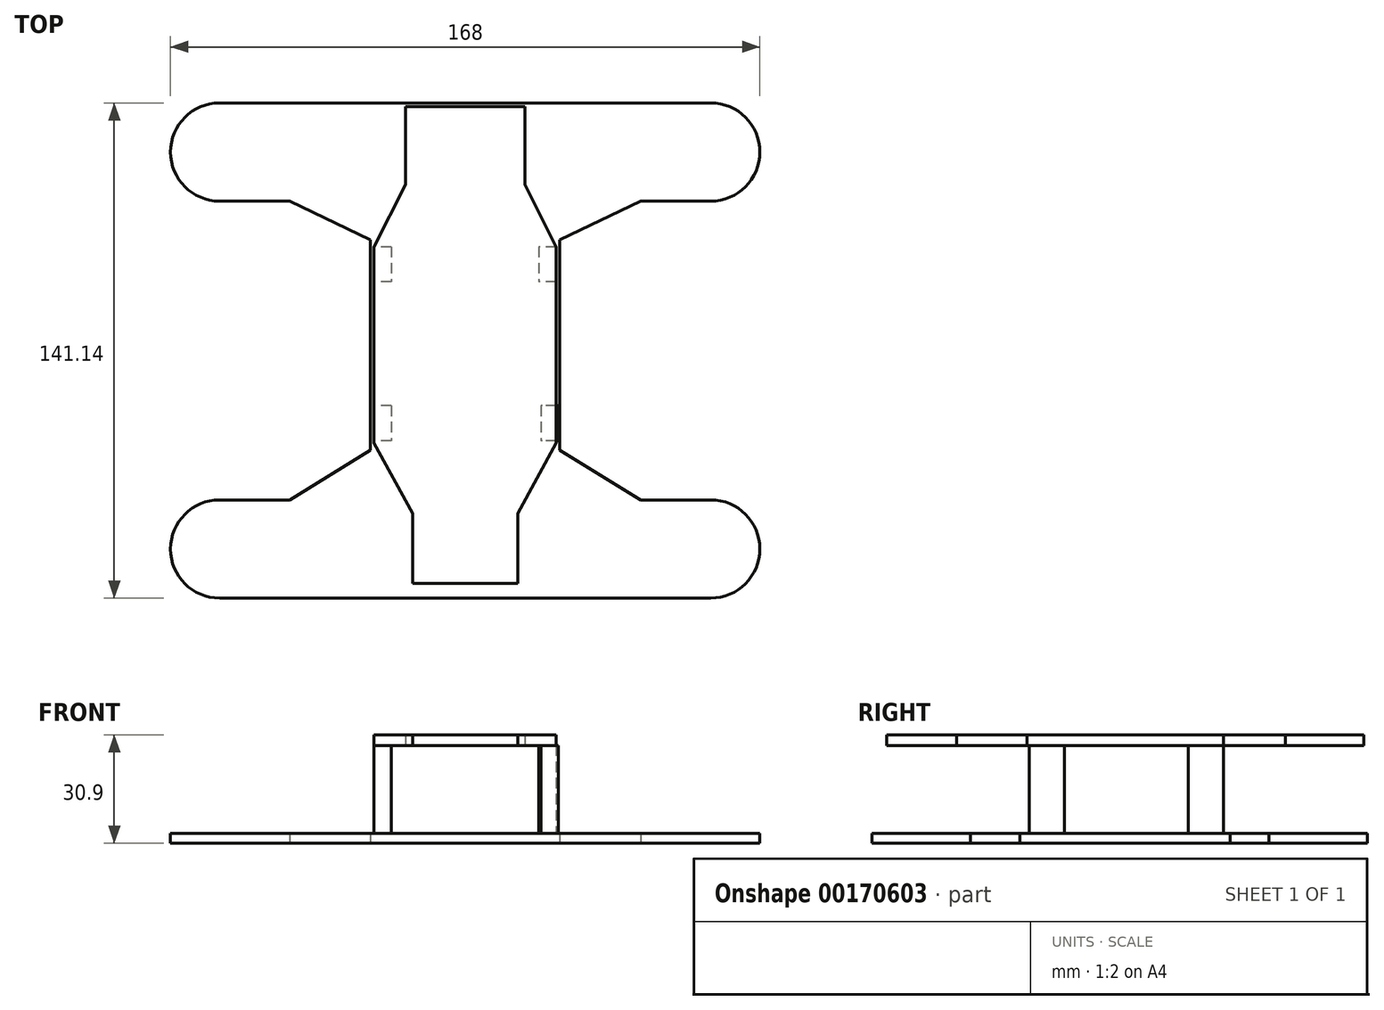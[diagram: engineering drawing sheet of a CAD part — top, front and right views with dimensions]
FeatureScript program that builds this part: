
annotation { "Feature Type Name" : "Feature", "Feature Type Description" : "" }
export const myFeature = defineFeature(function(context is Context, id is Id, definition is map)
    precondition{}
    {
        {
            var Q0;
            Q0=qCreatedBy(makeId("Top.planeOp"),FACE);
            var sketch = newSketch(context, id + "F0", { "sketchPlane" : qUnion([Q0])});
            skArc(sketch, "E0", {"start": v(-70, 69) * mm, "mid": v(-84, 55) * mm, "end": v(-70, 41) * mm});
            skArc(sketch, "E1", {"start": v(70, 41) * mm, "mid": v(84, 55) * mm, "end": v(70, 69) * mm});
            skArc(sketch, "E2", {"start": v(70, -72.14) * mm, "mid": v(84, -58.14) * mm, "end": v(70, -44.14) * mm});
            skArc(sketch, "E3", {"start": v(-70, -44.14) * mm, "mid": v(-84, -58.14) * mm, "end": v(-70, -72.14) * mm});
            skCircle(sketch, "E4", {"center": v(-70, 55) * mm, "radius": 50.8 * mm, "construction": true});
            skCircle(sketch, "E5", {"center": v(70, 55) * mm, "radius": 50.8 * mm, "construction": true});
            skCircle(sketch, "E6", {"center": v(70, -58.14) * mm, "radius": 50.8 * mm, "construction": true});
            skCircle(sketch, "E7", {"center": v(-70, -58.14) * mm, "radius": 50.8 * mm, "construction": true});
            skLineSegment(sketch, "E8", {"start": v(-70, 69) * mm, "end": v(70, 69) * mm});
            skLineSegment(sketch, "E9", {"start": v(-70, 41) * mm, "end": v(-50, 41) * mm});
            skLineSegment(sketch, "E10", {"start": v(-70, -44.14) * mm, "end": v(-50, -44.14) * mm});
            skLineSegment(sketch, "E11", {"start": v(-70, -72.14) * mm, "end": v(70, -72.14) * mm});
            skLineSegment(sketch, "E12.left", {"start": v(-27, 30) * mm, "end": v(-27, -30) * mm});
            skLineSegment(sketch, "E12.right", {"start": v(27, 30) * mm, "end": v(27, -30) * mm});
            skLineSegment(sketch, "E13.trimOffspring", {"start": v(-50, 41) * mm, "end": v(-27, 30) * mm});
            skLineSegment(sketch, "E14.trimOffspring", {"start": v(50, 41) * mm, "end": v(27, 30) * mm});
            skLineSegment(sketch, "E15.trimOffspring", {"start": v(-50, -44.14) * mm, "end": v(-27, -30) * mm});
            skLineSegment(sketch, "E16.trimOffspring", {"start": v(50, 41) * mm, "end": v(70, 41) * mm});
            skLineSegment(sketch, "E17", {"start": v(70, -44.14) * mm, "end": v(50, -44.14) * mm});
            skLineSegment(sketch, "E18", {"start": v(27, -30) * mm, "end": v(50, -44.14) * mm});
            skLineSegment(sketch, "E19.left", {"start": v(-84, 80.95) * mm, "end": v(-84, -83.14) * mm, "construction": true});
            skLineSegment(sketch, "E19.right", {"start": v(84, 80.95) * mm, "end": v(84, -83.14) * mm, "construction": true});
            skSolve(sketch);
        }
        {
            var Q0;
            Q0 = qSketchRegion(id + "F0", true);
            extrude(context, id + "F1", {"entities" : qUnion([Q0]), "depth" : 2.9 * mm});
        }
        {
            var Q0;
            Q0=makeQuery(id+"F1.opExtrude","CAP_FACE",FACE,{"disambiguationData":[OSD([sQuery(id+"F0.wireOp",EDGE,"E0"),sQuery(id+"F0.wireOp",EDGE,"E1"),sQuery(id+"F0.wireOp",EDGE,"E2"),sQuery(id+"F0.wireOp",EDGE,"E3"),sQuery(id+"F0.wireOp",EDGE,"E8"),sQuery(id+"F0.wireOp",EDGE,"E9"),sQuery(id+"F0.wireOp",EDGE,"E10"),sQuery(id+"F0.wireOp",EDGE,"E11"),sQuery(id+"F0.wireOp",EDGE,"E12.left"),sQuery(id+"F0.wireOp",EDGE,"E12.right"),sQuery(id+"F0.wireOp",EDGE,"E13.trimOffspring"),sQuery(id+"F0.wireOp",EDGE,"E14.trimOffspring"),sQuery(id+"F0.wireOp",EDGE,"E15.trimOffspring"),sQuery(id+"F0.wireOp",EDGE,"E16.trimOffspring"),sQuery(id+"F0.wireOp",EDGE,"E17"),sQuery(id+"F0.wireOp",EDGE,"E18")])],"isStart":false});
            cPlane(context, id + "F2", {"entities" : qUnion([Q0]), "cplaneType" : CPlaneType.OFFSET, "offset" : 25 * mm, "width" : 150 * mm, "height" : 150 * mm});
        }
        {
            var Q0;
            Q0=qCreatedBy(id+"F2.planeOp",FACE);
            var sketch = newSketch(context, id + "F3", { "sketchPlane" : qUnion([Q0])});
            skLineSegment(sketch, "E20.left", {"start": v(-26, 28) * mm, "end": v(-26, -28) * mm});
            skLineSegment(sketch, "E20.right", {"start": v(26, 28) * mm, "end": v(26, -28) * mm});
            skLineSegment(sketch, "E21.bottom", {"start": v(-17, 68) * mm, "end": v(17, 68) * mm});
            skLineSegment(sketch, "E21.left", {"start": v(-17, 68) * mm, "end": v(-17, 45.69) * mm});
            skLineSegment(sketch, "E21.right", {"start": v(17, 68) * mm, "end": v(17, 45.69) * mm});
            skLineSegment(sketch, "E22.top", {"start": v(-15, -68) * mm, "end": v(15, -68) * mm});
            skLineSegment(sketch, "E22.left", {"start": v(-15, -48) * mm, "end": v(-15, -68) * mm});
            skLineSegment(sketch, "E22.right", {"start": v(15, -48) * mm, "end": v(15, -68) * mm});
            skLineSegment(sketch, "E23", {"start": v(15, -48) * mm, "end": v(26, -28) * mm});
            skLineSegment(sketch, "E24", {"start": v(-26, -28) * mm, "end": v(-15, -48) * mm});
            skPoint(sketch, "E25.orphan", {"position": v(-15, -28) * mm});
            skPoint(sketch, "E26.orphan", {"position": v(15, -28) * mm});
            skLineSegment(sketch, "E27", {"start": v(-17, 45.69) * mm, "end": v(-26, 28) * mm});
            skLineSegment(sketch, "E28", {"start": v(17, 45.69) * mm, "end": v(26, 28) * mm});
            skSolve(sketch);
        }
        {
            var Q0;
            Q0=makeQuery(id+"F3.imprint","IMPRINT",FACE,{"disambiguationData":[TD([[makeQuery(id+"F3.imprint","IMPRINT",EDGE,{"derivedFrom":sQuery(id+"F3.wireOp",EDGE,"E20.left")}),1.0]])]});
            extrude(context, id + "F4", {"entities" : qUnion([Q0]), "depth" : 3 * mm});
        }
        {
            var Q0;
            Q0=makeQuery(id+"F4.opExtrude","SWEPT_FACE",FACE,{"disambiguationData":[OSD([sQuery(id+"F3.wireOp",EDGE,"E20.left")])]});
            var sketch = newSketch(context, id + "F5", { "sketchPlane" : qUnion([Q0])});
            skLineSegment(sketch, "E29.bottom", {"start": v(-28, 27.9) * mm, "end": v(-18, 27.9) * mm});
            skLineSegment(sketch, "E29.top", {"start": v(-28, 2.9) * mm, "end": v(-18, 2.9) * mm});
            skLineSegment(sketch, "E29.left", {"start": v(-28, 27.9) * mm, "end": v(-28, 2.9) * mm});
            skLineSegment(sketch, "E29.right", {"start": v(-18, 27.9) * mm, "end": v(-18, 2.9) * mm});
            skSolve(sketch);
        }
        {
            var Q0;
            Q0=makeQuery(id+"F5.imprint","IMPRINT",FACE,{"disambiguationData":[TD([[makeQuery(id+"F5.imprint","IMPRINT",EDGE,{"derivedFrom":sQuery(id+"F5.wireOp",EDGE,"E29.bottom")}),-1.0]])]});
            extrude(context, id + "F6", {"entities" : qUnion([Q0]), "oppositeDirection" : true, "depth" : 5 * mm});
        }
        {
            var Q0;
            Q0=makeQuery(id+"F6.opExtrude","SWEPT_BODY",BODY,{"disambiguationData":[OSD([sQuery(id+"F5.wireOp",EDGE,"E29.bottom"),sQuery(id+"F5.wireOp",EDGE,"E29.top"),sQuery(id+"F5.wireOp",EDGE,"E29.left"),sQuery(id+"F5.wireOp",EDGE,"E29.right")])]});
            transform(context, id + "F7", {"entities" : qUnion([Q0]), "transformType" : TransformType.TRANSLATION_3D, "dx" : 0 * mm, "dy" : -45.3 * mm, "dz" : 0 * mm, "makeCopy" : true});
        }
        {
            var Q0;
            Q0=makeQuery(id+"F7.opPattern","COPY",BODY,{"derivedFrom":makeQuery(id+"F6.opExtrude","SWEPT_BODY",BODY,{"disambiguationData":[OSD([sQuery(id+"F5.wireOp",EDGE,"E29.bottom"),sQuery(id+"F5.wireOp",EDGE,"E29.top"),sQuery(id+"F5.wireOp",EDGE,"E29.left"),sQuery(id+"F5.wireOp",EDGE,"E29.right")])]}),"instanceName":"1"});
            transform(context, id + "F8", {"entities" : qUnion([Q0]), "transformType" : TransformType.TRANSLATION_3D, "dx" : 47.6 * mm, "dy" : 0 * mm, "dz" : 0 * mm, "makeCopy" : true});
        }
        {
            var Q0;
            Q0=makeQuery(id+"F6.opExtrude","SWEPT_BODY",BODY,{"disambiguationData":[OSD([sQuery(id+"F5.wireOp",EDGE,"E29.bottom"),sQuery(id+"F5.wireOp",EDGE,"E29.top"),sQuery(id+"F5.wireOp",EDGE,"E29.left"),sQuery(id+"F5.wireOp",EDGE,"E29.right")])]});
            transform(context, id + "F9", {"entities" : qUnion([Q0]), "transformType" : TransformType.TRANSLATION_3D, "dx" : 47 * mm, "dy" : 0 * mm, "dz" : 0 * mm, "makeCopy" : true});
        }
    });
